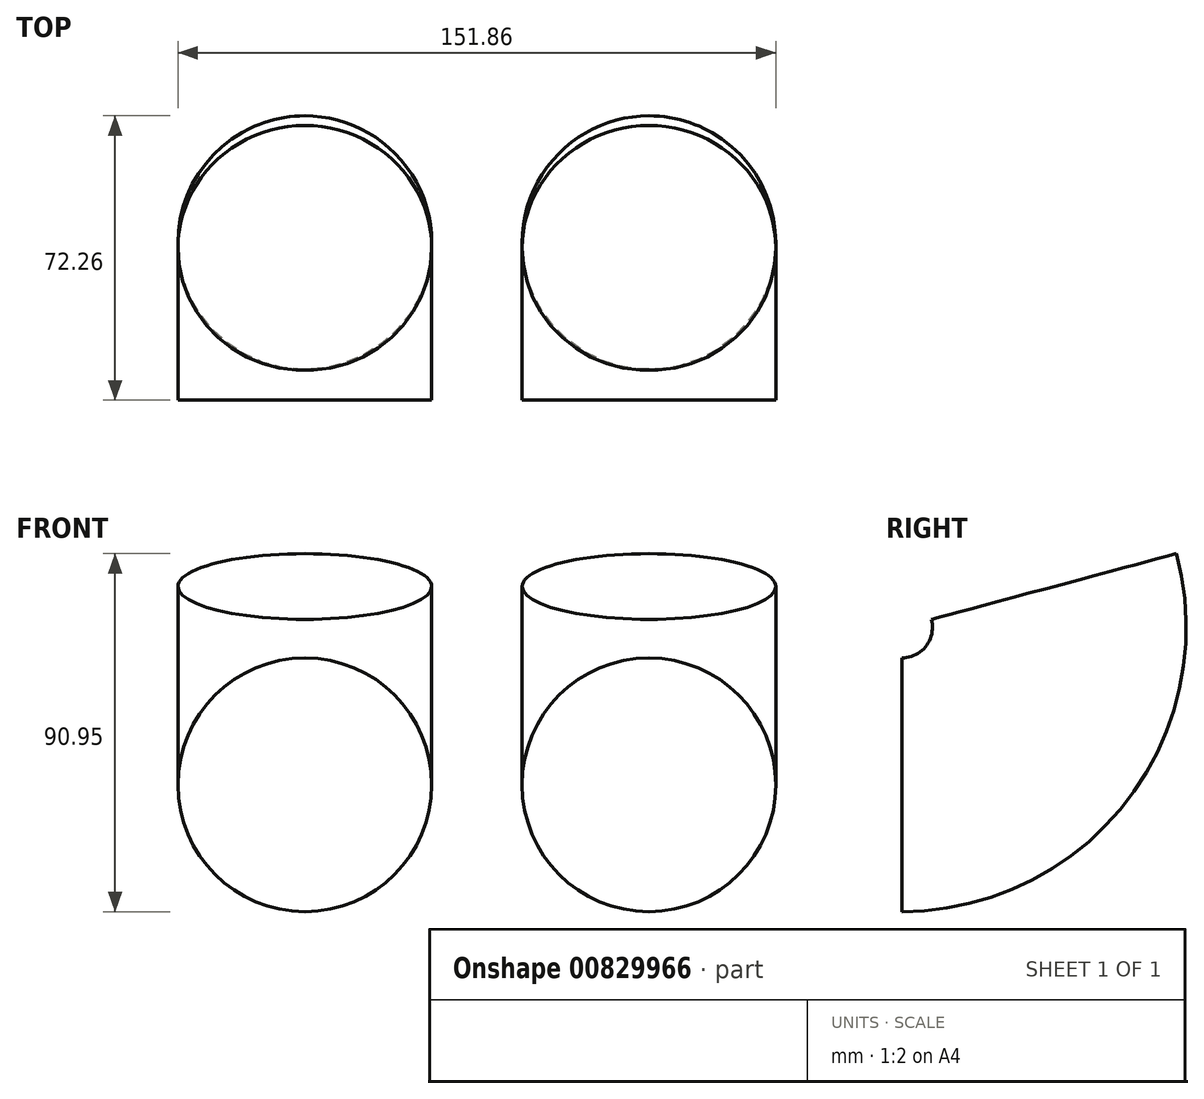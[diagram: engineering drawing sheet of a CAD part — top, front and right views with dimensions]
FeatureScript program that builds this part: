
annotation { "Feature Type Name" : "Feature", "Feature Type Description" : "" }
export const myFeature = defineFeature(function(context is Context, id is Id, definition is map)
    precondition{}
    {
        {
            var Q0;
            Q0=qCreatedBy(makeId("Front.planeOp"),FACE);
            var sketch = newSketch(context, id + "F0", { "sketchPlane" : qUnion([Q0])});
            skCircle(sketch, "E0", {"center": v(-43.7, -4.17) * mm, "radius": 32.23 * mm});
            skLineSegment(sketch, "E1.bottom", {"start": v(3.19, 35.86) * mm, "end": v(50.73, 35.86) * mm});
            skLineSegment(sketch, "E1.top", {"start": v(3.19, 9.4) * mm, "end": v(50.73, 9.4) * mm});
            skLineSegment(sketch, "E1.left", {"start": v(3.19, 35.86) * mm, "end": v(3.19, 9.4) * mm});
            skLineSegment(sketch, "E1.right", {"start": v(50.73, 35.86) * mm, "end": v(50.73, 9.4) * mm});
            skSolve(sketch);
        }
        {
            var Q0;
            Q0=makeQuery(id+"F0.imprint","IMPRINT",FACE,{"disambiguationData":[TD([[makeQuery(id+"F0.imprint","IMPRINT",EDGE,{"derivedFrom":sQuery(id+"F0.wireOp",EDGE,"E0")}),1.0]])]});
            var Q1;
            Q1=sQuery(id+"F0.wireOp",EDGE,"E1.bottom");
            revolve(context, id + "F1", {"surfaceOperationType" : NewSurfaceOperationType.NEW, "entities" : qUnion([Q0]), "axis" : qUnion([Q1]), "revolveType" : RevolveType.ONE_DIRECTION, "angle" : 105 * degree});
        }
        {
            var Q0;
            Q0=makeQuery(id+"F1.opRevolve","SWEPT_BODY",BODY,{"disambiguationData":[OSD([sQuery(id+"F0.wireOp",EDGE,"E0")])]});
            var Q1;
            Q1=qCreatedBy(makeId("Right.planeOp"),FACE);
            mirror(context, id + "F2", {"entities" : qUnion([Q0]), "mirrorPlane" : qUnion([Q1])});
        }
    });
